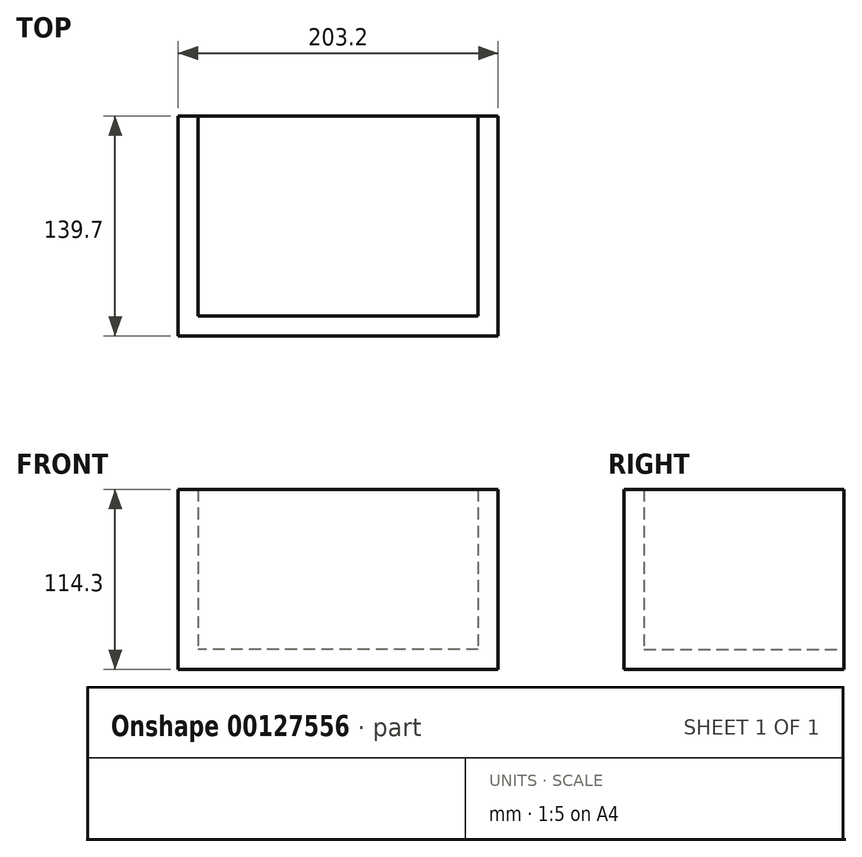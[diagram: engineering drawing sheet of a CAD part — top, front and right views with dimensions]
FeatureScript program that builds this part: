
annotation { "Feature Type Name" : "Feature", "Feature Type Description" : "" }
export const myFeature = defineFeature(function(context is Context, id is Id, definition is map)
    precondition{}
    {
        {
            var Q0;
            Q0=qCreatedBy(makeId("Front.planeOp"),FACE);
            var sketch = newSketch(context, id + "F0", { "sketchPlane" : qUnion([Q0])});
            skLineSegment(sketch, "E0.bottom", {"start": v(101.6, 57.15) * mm, "end": v(-101.6, 57.15) * mm});
            skLineSegment(sketch, "E0.top", {"start": v(101.6, -57.15) * mm, "end": v(-101.6, -57.15) * mm});
            skLineSegment(sketch, "E0.left", {"start": v(101.6, 57.15) * mm, "end": v(101.6, -57.15) * mm});
            skLineSegment(sketch, "E0.right", {"start": v(-101.6, 57.15) * mm, "end": v(-101.6, -57.15) * mm});
            skPoint(sketch, "E0.middle", {"position": v(0, 0) * mm});
            skSolve(sketch);
        }
        {
            var Q0;
            Q0 = qSketchRegion(id + "F0", true);
            extrude(context, id + "F1", {"entities" : qUnion([Q0]), "endBound" : BoundingType.SYMMETRIC, "depth" : 139.7 * mm});
        }
        {
            var Q0;
            Q0=makeQuery(id+"F1.opExtrude","SWEPT_FACE",FACE,{"disambiguationData":[OSD([sQuery(id+"F0.wireOp",EDGE,"E0.bottom")])]});
            var Q1;
            Q1=makeQuery(id+"F1.opExtrude","CAP_FACE",FACE,{"disambiguationData":[OSD([sQuery(id+"F0.wireOp",EDGE,"E0.bottom"),sQuery(id+"F0.wireOp",EDGE,"E0.top"),sQuery(id+"F0.wireOp",EDGE,"E0.left"),sQuery(id+"F0.wireOp",EDGE,"E0.right")])],"isStart":true});
            shell(context, id + "F2", {"entities" : qUnion([Q0, Q1]), "thickness" : 12.7 * mm});
        }
    });
